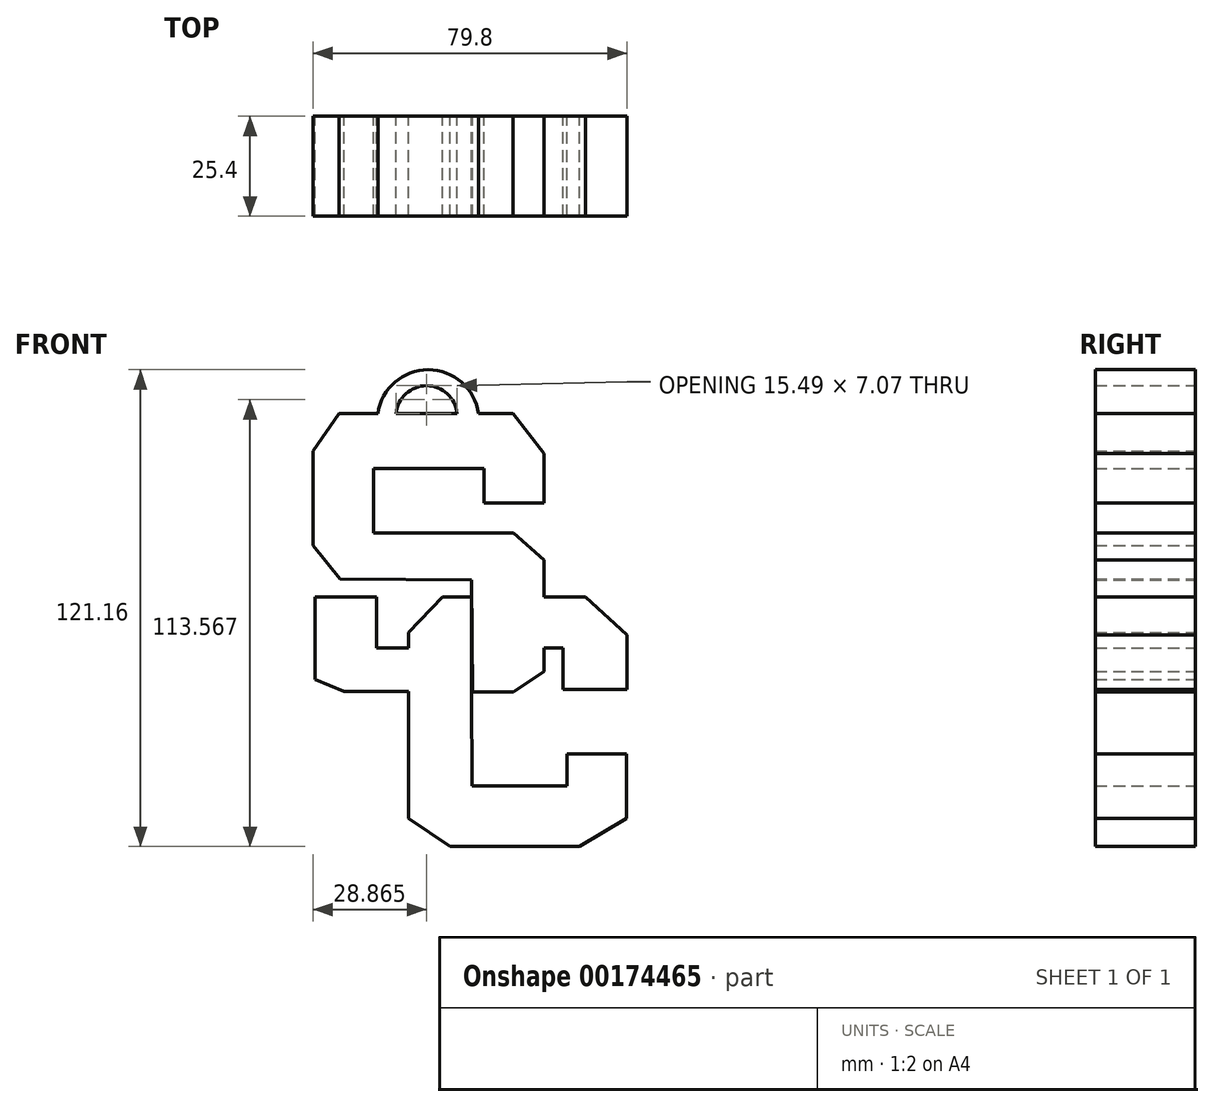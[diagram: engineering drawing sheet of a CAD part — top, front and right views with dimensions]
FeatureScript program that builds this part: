
annotation { "Feature Type Name" : "Feature", "Feature Type Description" : "" }
export const myFeature = defineFeature(function(context is Context, id is Id, definition is map)
    precondition{}
    {
        {
            var Q0;
            Q0=qCreatedBy(makeId("Front.planeOp"),FACE);
            var sketch = newSketch(context, id + "F0", { "sketchPlane" : qUnion([Q0])});
            skLineSegment(sketch, "E0", {"start": v(-22.06, 65.51) * mm, "end": v(22.13, 65.51) * mm});
            skLineSegment(sketch, "E1", {"start": v(22.13, 65.51) * mm, "end": v(30.01, 55.4) * mm});
            skLineSegment(sketch, "E2", {"start": v(30.01, 55.4) * mm, "end": v(30.01, 42.82) * mm});
            skLineSegment(sketch, "E3", {"start": v(30.01, 42.82) * mm, "end": v(14.79, 42.82) * mm});
            skLineSegment(sketch, "E4", {"start": v(14.79, 42.82) * mm, "end": v(14.79, 51.6) * mm});
            skLineSegment(sketch, "E5", {"start": v(14.79, 51.6) * mm, "end": v(-13.32, 51.6) * mm});
            skLineSegment(sketch, "E6", {"start": v(-13.32, 51.6) * mm, "end": v(-13.32, 35.2) * mm});
            skLineSegment(sketch, "E7", {"start": v(-13.32, 35.2) * mm, "end": v(13.18, 35.2) * mm});
            skLineSegment(sketch, "E8", {"start": v(13.18, 35.2) * mm, "end": v(18.74, 35.2) * mm});
            skLineSegment(sketch, "E9", {"start": v(18.74, 35.2) * mm, "end": v(22.25, 35.2) * mm});
            skLineSegment(sketch, "E10", {"start": v(22.25, 35.2) * mm, "end": v(30.01, 28.32) * mm});
            skLineSegment(sketch, "E11", {"start": v(30.01, 28.32) * mm, "end": v(30.01, 0) * mm});
            skLineSegment(sketch, "E12", {"start": v(30.01, 0) * mm, "end": v(22.25, -5.2) * mm});
            skLineSegment(sketch, "E13", {"start": v(22.25, -5.2) * mm, "end": v(11.78, -5.2) * mm});
            skLineSegment(sketch, "E14", {"start": v(11.57, -5.2) * mm, "end": v(11.57, 23.5) * mm});
            skLineSegment(sketch, "E15", {"start": v(11.42, 23.5) * mm, "end": v(-16.25, 23.5) * mm});
            skLineSegment(sketch, "E16", {"start": v(-16.25, 23.5) * mm, "end": v(-21.77, 23.5) * mm});
            skLineSegment(sketch, "E17", {"start": v(-22.06, 65.51) * mm, "end": v(-28.7, 56) * mm});
            skLineSegment(sketch, "E18", {"start": v(-28.7, 56) * mm, "end": v(-28.66, 32) * mm});
            skLineSegment(sketch, "E19", {"start": v(-28.66, 32) * mm, "end": v(-21.77, 23.5) * mm});
            skLineSegment(sketch, "E20", {"start": v(30.01, 18.9) * mm, "end": v(40.6, 18.9) * mm});
            skLineSegment(sketch, "E21", {"start": v(40.6, 18.9) * mm, "end": v(51.1, 9.28) * mm});
            skLineSegment(sketch, "E22", {"start": v(51.1, 9.28) * mm, "end": v(51.1, -4.62) * mm});
            skLineSegment(sketch, "E23", {"start": v(51.1, -4.62) * mm, "end": v(34.84, -4.62) * mm});
            skLineSegment(sketch, "E24", {"start": v(34.84, -4.62) * mm, "end": v(34.84, 6.02) * mm});
            skLineSegment(sketch, "E25", {"start": v(34.84, 6.02) * mm, "end": v(30.01, 6.02) * mm});
            skLineSegment(sketch, "E26", {"start": v(4.24, 18.9) * mm, "end": v(-4.4, 9.88) * mm});
            skLineSegment(sketch, "E27", {"start": v(-4.4, 9.88) * mm, "end": v(-4.4, -37.41) * mm});
            skLineSegment(sketch, "E28", {"start": v(11.57, 18.9) * mm, "end": v(4.24, 18.9) * mm});
            skLineSegment(sketch, "E29", {"start": v(-4.4, 6.02) * mm, "end": v(-12.52, 6.02) * mm});
            skLineSegment(sketch, "E30", {"start": v(-28.1, 18.9) * mm, "end": v(-12.52, 18.9) * mm});
            skLineSegment(sketch, "E31", {"start": v(-28.1, 18.9) * mm, "end": v(-28.1, -1.98) * mm});
            skLineSegment(sketch, "E32", {"start": v(-4.4, -5.06) * mm, "end": v(-20.79, -5.06) * mm});
            skLineSegment(sketch, "E33", {"start": v(-20.79, -5.06) * mm, "end": v(-28.1, -1.98) * mm});
            skLineSegment(sketch, "E34", {"start": v(-12.52, 19.25) * mm, "end": v(-12.52, 6.02) * mm});
            skLineSegment(sketch, "E35", {"start": v(-12.52, 6.02) * mm, "end": v(-12.52, 6.02) * mm});
            skLineSegment(sketch, "E36", {"start": v(-4.4, -37.41) * mm, "end": v(6.13, -44.52) * mm});
            skLineSegment(sketch, "E37", {"start": v(6.13, -44.52) * mm, "end": v(39, -44.52) * mm});
            skLineSegment(sketch, "E38", {"start": v(39, -44.52) * mm, "end": v(50.98, -37.41) * mm});
            skLineSegment(sketch, "E39", {"start": v(50.98, -37.41) * mm, "end": v(50.98, -20.91) * mm});
            skLineSegment(sketch, "E40", {"start": v(50.98, -20.91) * mm, "end": v(35.86, -20.91) * mm});
            skLineSegment(sketch, "E41", {"start": v(35.86, -20.91) * mm, "end": v(35.86, -29.13) * mm});
            skLineSegment(sketch, "E42", {"start": v(35.86, -29.13) * mm, "end": v(11.75, -29.13) * mm});
            skLineSegment(sketch, "E43", {"start": v(11.75, -29.13) * mm, "end": v(11.57, -5.2) * mm});
            skLineSegment(sketch, "E44", {"start": v(11.78, -5.2) * mm, "end": v(11.57, 23.5) * mm});
            skLineSegment(sketch, "E45", {"start": v(11.6, 23.27) * mm, "end": v(-21.77, 23.5) * mm});
            skLineSegment(sketch, "E46", {"start": v(-21.77, 23.5) * mm, "end": v(-28.66, 32) * mm});
            skArc(sketch, "E47", {"start": v(7.91, 65.51) * mm, "mid": v(0.16, 72.58) * mm, "end": v(-7.58, 65.51) * mm});
            skArc(sketch, "E48", {"start": v(13.35, 65.51) * mm, "mid": v(0.58, 76.64) * mm, "end": v(-12.2, 65.51) * mm});
            skSolve(sketch);
        }
        {
            var Q0;
            Q0 = qSketchRegion(id + "F0", true);
            extrude(context, id + "F1", {"entities" : qUnion([Q0]), "depth" : 25.4 * mm});
        }
    });
